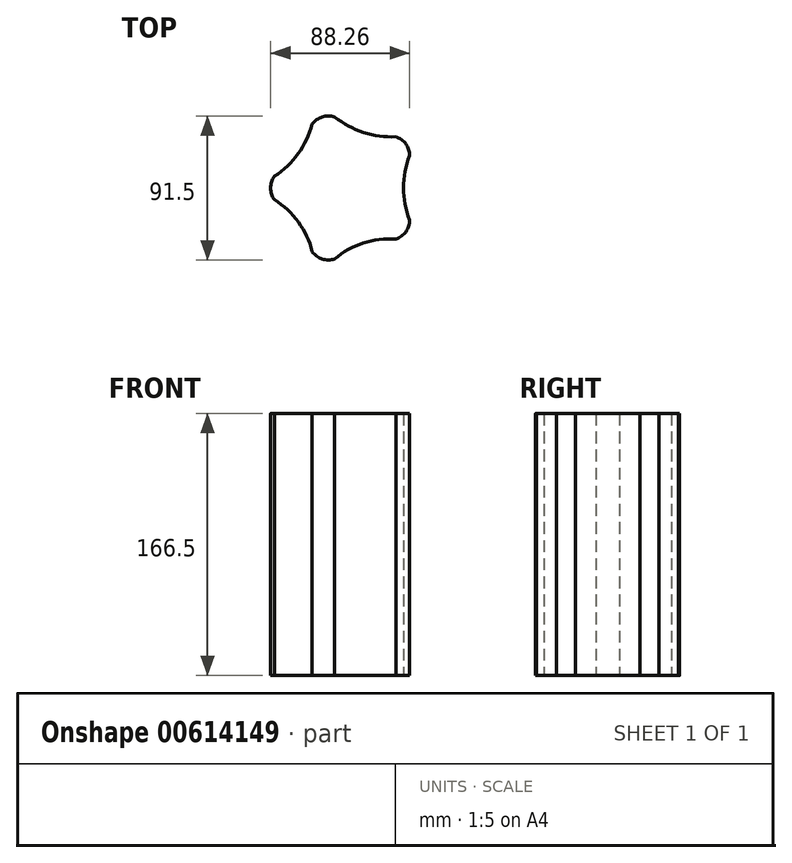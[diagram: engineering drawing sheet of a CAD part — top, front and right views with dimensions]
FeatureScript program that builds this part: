
annotation { "Feature Type Name" : "Feature", "Feature Type Description" : "" }
export const myFeature = defineFeature(function(context is Context, id is Id, definition is map)
    precondition{}
    {
        {
            var Q0;
            Q0=qCreatedBy(makeId("Top.planeOp"),FACE);
            var sketch = newSketch(context, id + "F0", { "sketchPlane" : qUnion([Q0])});
            skPoint(sketch, "E0.0.midPoint", {"position": v(40.81, 0) * mm});
            skPoint(sketch, "E1.visualSharp", {"position": v(-15.59, 47.98) * mm});
            skArc(sketch, "E1.filletArc", {"start": v(-6.81, 45.12) * mm, "mid": v(-14.66, 45.12) * mm, "end": v(-21.01, 40.51) * mm});
            skPoint(sketch, "E2.visualSharp", {"position": v(40.81, 29.65) * mm});
            skArc(sketch, "E2.filletArc", {"start": v(40.81, 20.42) * mm, "mid": v(38.39, 27.89) * mm, "end": v(32.04, 32.5) * mm});
            skPoint(sketch, "E3.visualSharp", {"position": v(40.81, -29.65) * mm});
            skArc(sketch, "E3.filletArc", {"start": v(32.04, -32.5) * mm, "mid": v(38.39, -27.89) * mm, "end": v(40.81, -20.42) * mm});
            skPoint(sketch, "E4.visualSharp", {"position": v(-15.59, -47.98) * mm});
            skArc(sketch, "E4.filletArc", {"start": v(-21.01, -40.51) * mm, "mid": v(-14.66, -45.12) * mm, "end": v(-6.81, -45.12) * mm});
            skPoint(sketch, "E5.visualSharp", {"position": v(-50.45, 0) * mm});
            skArc(sketch, "E5.filletArc", {"start": v(-45.02, 7.46) * mm, "mid": v(-47.45, 0) * mm, "end": v(-45.02, -7.46) * mm});
            skArc(sketch, "E6", {"start": v(-6.81, 45.12) * mm, "mid": v(11.47, 35.3) * mm, "end": v(32.04, 32.5) * mm});
            skArc(sketch, "E7", {"start": v(40.81, 20.42) * mm, "mid": v(36.94, 0) * mm, "end": v(40.81, -20.42) * mm});
            skArc(sketch, "E8", {"start": v(32.04, -32.5) * mm, "mid": v(11.4, -35.06) * mm, "end": v(-6.81, -45.12) * mm});
            skArc(sketch, "E9", {"start": v(-21.01, -40.51) * mm, "mid": v(-29.84, -21.68) * mm, "end": v(-45.02, -7.46) * mm});
            skArc(sketch, "E10", {"start": v(-45.02, 7.46) * mm, "mid": v(-29.92, 21.73) * mm, "end": v(-21.01, 40.51) * mm});
            skPoint(sketch, "E11.center.orphan", {"position": v(0, 0) * mm});
            skSolve(sketch);
        }
        {
            var Q0;
            Q0 = qSketchRegion(id + "F0", true);
            extrude(context, id + "F1", {"entities" : qUnion([Q0]), "depth" : 166.5 * mm, "offsetDistance" : 25.4 * mm});
        }
    });
